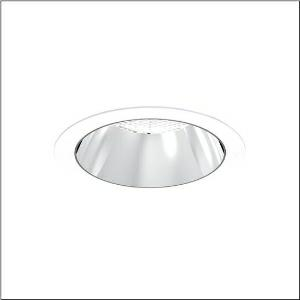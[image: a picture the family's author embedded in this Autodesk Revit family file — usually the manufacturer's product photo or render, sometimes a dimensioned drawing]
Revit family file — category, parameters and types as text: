
# Revit family: lunis_21_xl_51db15tf91c
name_source: partatom
category: Lighting Fixtures
units: mm (PartAtom-declared; Revit-internal decimal feet)

## family parameters
Cut with Voids When Loaded = No
Host = Face
Light Source = No
Part Type = Normal
Room Calculation Point = No
Round Connector Dimension = Use Diameter
Shared = No

## types (1)
- --- (1 x LED 3000 K ... 6500 K, 4150 lm, 25.4 W, 4000K)
    Apparent Load = 25 VA
    CIE Flux Codes = 92 100 100 100 100
    Color Rendering = 80
    Color Temperature = 4000K
    Default Elevation = 1800 mm
    Description = Lunis 21,  XL, downlight, light control with lens, of PMMA, anti glare with reflector, of aluminium, highly specular, light emission: direct distribution, LED rated luminous flux: 4.150lm, light colour: 8tw, with terminal, 5-pole, mains connection: 220..240V, AC/DC, 0/50..60Hz, housing, round, of diecast aluminium, traffic white (RAL 9016), diameter: 230mm, clamping range: 1..40mm, protection rating (complete): IP20, protection rating (on room side): IP54, insulation class (complete): insulation class II (safety insulation), certification: CE, impact resistance: IK03, packaging unit: 1 piece
    Height = 0 mm  [stored 0 ft]
    Lamp = 1 x LED 3000 K ... 6500 K
    Lamp Light Flux = 4150 lm
    Lamp Power = 25.4 W
    Lamp count = 1
    Length = 230 mm
    Luminous efficacy = 163 lm/W
    Manufacturer = Siteco
    ModVariant = No
    Model = 51DB15TF91C
    Mounting Place = Ceiling
    Mounting Type = Recessed
    Number of Poles = 1
    OnlyDefault = Yes
    Power Factor = 1
    Product Name = Lunis 21 XL
    Product group = downlight
    ProductGroupID = 400
    Protection Class = Protection class II
    Protection Degree = IP 20
    RLX_Detail_Level = 1
    RLX_Emergency_Light_Flux = 0 lm
    RLX_Emergency_Type = 0
    RLX_Emergency_Type_DB = No
    RlxData = <blob elided: 18837 chars, md5=7ed223fd>
    Socket = socket
    Standby Power = 0 W
    System Light Flux = 4150 lm
    System Power = 25 W
    Type Comments = individual setting: CCT=4000K, colour temperature 4000K, luminous flux: 100 % | (ON | ON | OFF | OFF) | 700 mA
    Type Image = l_1291156.jpg
    URL = http://relux.com
    VarID = @adj_020240
    Voltage = 0 V
    Weight = 0.00 kg
    Width = 0 mm  [stored 0 ft]

note: [stored X ft] marks values corroborated as IEEE doubles in the binary element streams (Revit-internal decimal feet)

## geometry (parser evidence)
native form markers: Blend x4, Sweep x9
no freeform markers — native parametric forms only
